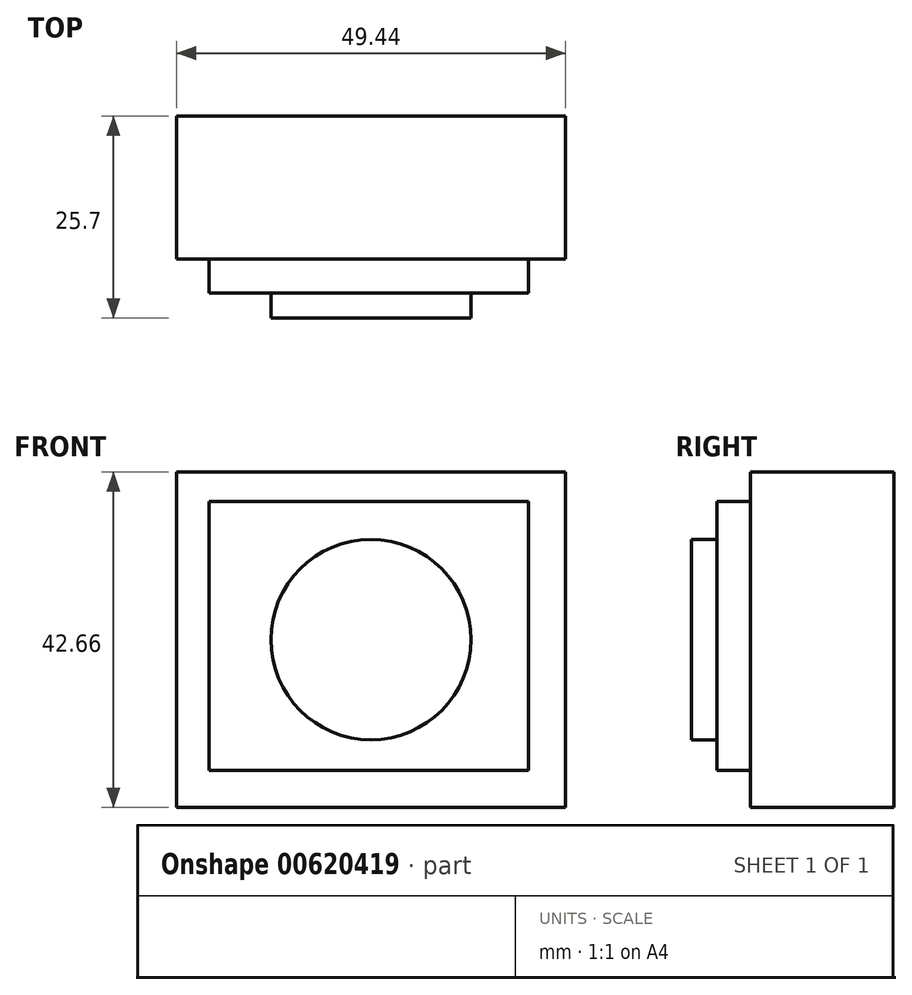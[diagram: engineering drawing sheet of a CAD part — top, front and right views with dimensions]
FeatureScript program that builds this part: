
annotation { "Feature Type Name" : "Feature", "Feature Type Description" : "" }
export const myFeature = defineFeature(function(context is Context, id is Id, definition is map)
    precondition{}
    {
        {
            var Q0;
            Q0=qCreatedBy(makeId("Front.planeOp"),FACE);
            var sketch = newSketch(context, id + "F0", { "sketchPlane" : qUnion([Q0])});
            skLineSegment(sketch, "E0.bottom", {"start": v(24.72, 21.33) * mm, "end": v(-24.72, 21.33) * mm});
            skLineSegment(sketch, "E0.top", {"start": v(24.72, -21.33) * mm, "end": v(-24.72, -21.33) * mm});
            skLineSegment(sketch, "E0.left", {"start": v(24.72, 21.33) * mm, "end": v(24.72, -21.33) * mm});
            skLineSegment(sketch, "E0.right", {"start": v(-24.72, 21.33) * mm, "end": v(-24.72, -21.33) * mm});
            skPoint(sketch, "E0.middle", {"position": v(0, 0) * mm});
            skSolve(sketch);
        }
        {
            var Q0;
            Q0=makeQuery(id+"F0.imprint","IMPRINT",FACE,{"disambiguationData":[TD([[makeQuery(id+"F0.imprint","IMPRINT",EDGE,{"derivedFrom":sQuery(id+"F0.wireOp",EDGE,"E0.bottom")}),1.0]])]});
            extrude(context, id + "F1", {"entities" : qUnion([Q0]), "depth" : 18.2 * mm, "offsetDistance" : 25 * mm});
        }
        {
            var Q0;
            Q0=makeQuery(id+"F1.opExtrude","CAP_FACE",FACE,{"disambiguationData":[OSD([sQuery(id+"F0.wireOp",EDGE,"E0.bottom"),sQuery(id+"F0.wireOp",EDGE,"E0.top"),sQuery(id+"F0.wireOp",EDGE,"E0.left"),sQuery(id+"F0.wireOp",EDGE,"E0.right")])],"isStart":false});
            var sketch = newSketch(context, id + "F2", { "sketchPlane" : qUnion([Q0])});
            skLineSegment(sketch, "E1.bottom", {"start": v(-20.58, 17.57) * mm, "end": v(20.02, 17.57) * mm});
            skLineSegment(sketch, "E1.top", {"start": v(-20.58, -16.63) * mm, "end": v(20.02, -16.63) * mm});
            skLineSegment(sketch, "E1.left", {"start": v(-20.58, 17.57) * mm, "end": v(-20.58, -16.63) * mm});
            skLineSegment(sketch, "E1.right", {"start": v(20.02, 17.57) * mm, "end": v(20.02, -16.63) * mm});
            skSolve(sketch);
        }
        {
            var Q0;
            Q0=makeQuery(id+"F2.imprint","IMPRINT",FACE,{"disambiguationData":[TD([[makeQuery(id+"F2.imprint","IMPRINT",EDGE,{"derivedFrom":sQuery(id+"F2.wireOp",EDGE,"E1.bottom")}),-1.0]])]});
            extrude(context, id + "F3", {"entities" : qUnion([Q0]), "operationType" : NewBodyOperationType.ADD, "depth" : 4.3 * mm, "offsetDistance" : 25 * mm});
        }
        {
            var Q0;
            Q0=makeQuery(id+"F3.opExtrude","CAP_FACE",FACE,{"disambiguationData":[OSD([sQuery(id+"F2.wireOp",EDGE,"E1.bottom"),sQuery(id+"F2.wireOp",EDGE,"E1.top"),sQuery(id+"F2.wireOp",EDGE,"E1.left"),sQuery(id+"F2.wireOp",EDGE,"E1.right")])],"isStart":false});
            var sketch = newSketch(context, id + "F4", { "sketchPlane" : qUnion([Q0])});
            skCircle(sketch, "E2", {"center": v(0, 0) * mm, "radius": 12.72 * mm});
            skSolve(sketch);
        }
        {
            var Q0;
            Q0=makeQuery(id+"F4.imprint","IMPRINT",FACE,{"disambiguationData":[TD([[makeQuery(id+"F4.imprint","IMPRINT",EDGE,{"derivedFrom":sQuery(id+"F4.wireOp",EDGE,"E2")}),1.0]])]});
            extrude(context, id + "F5", {"entities" : qUnion([Q0]), "operationType" : NewBodyOperationType.ADD, "depth" : 3.2 * mm, "offsetDistance" : 25 * mm});
        }
    });
